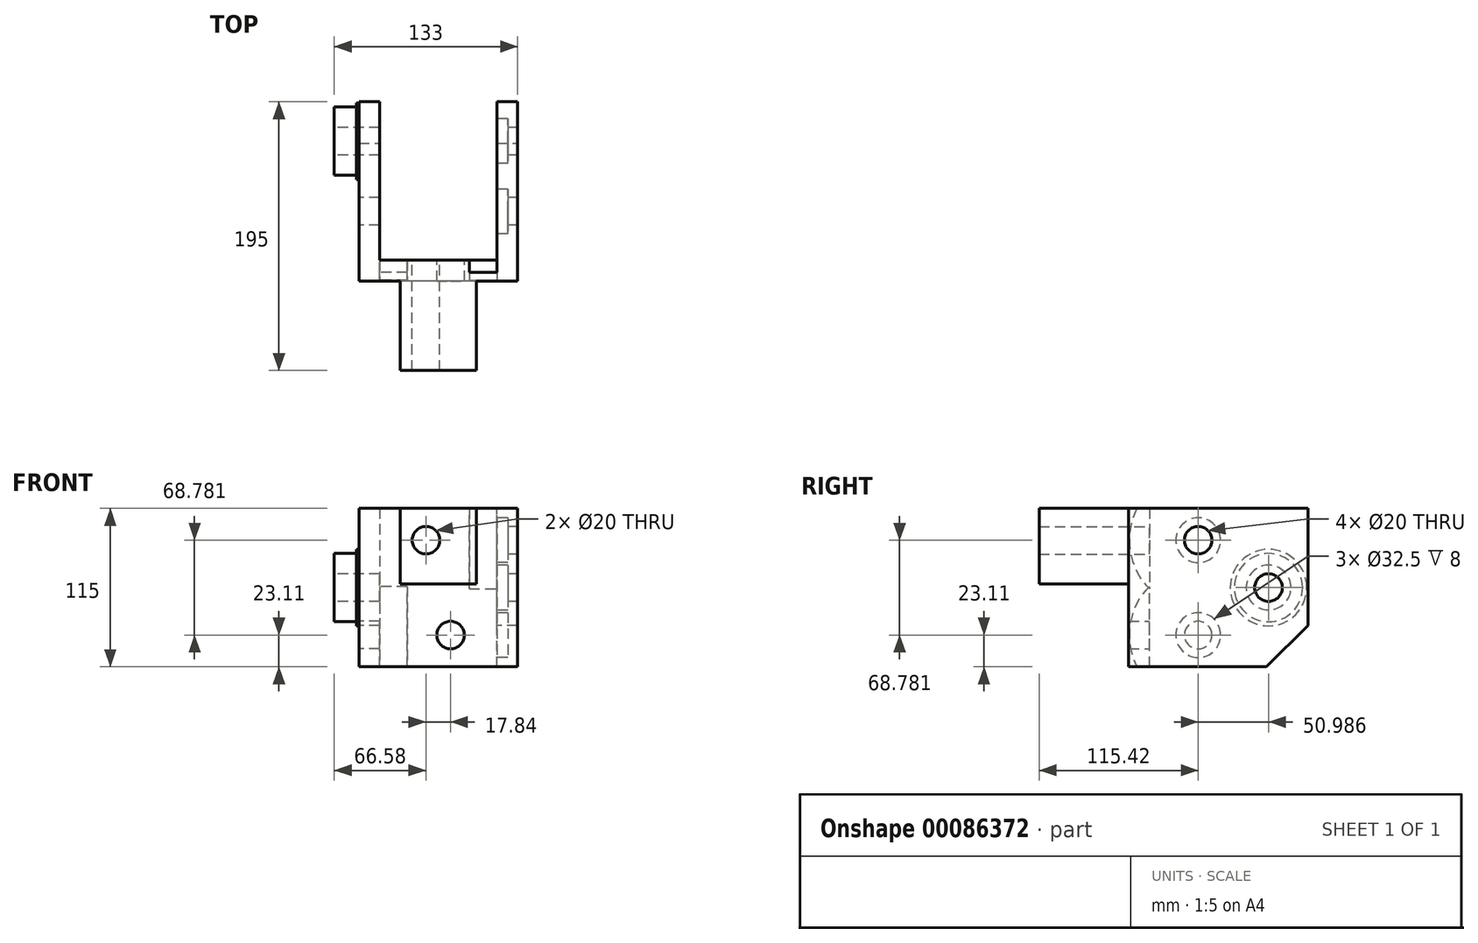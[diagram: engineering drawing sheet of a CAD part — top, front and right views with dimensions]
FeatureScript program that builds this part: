
annotation { "Feature Type Name" : "Feature", "Feature Type Description" : "" }
export const myFeature = defineFeature(function(context is Context, id is Id, definition is map)
    precondition{}
    {
        {
            assignVariable(context, id + "F0", {"name" : "Offset", "anyValue" : 85});
        }
        {
            var Q0;
            Q0=qCreatedBy(makeId("Right.planeOp"),FACE);
            var sketch = newSketch(context, id + "F1", { "sketchPlane" : qUnion([Q0])});
            skCircle(sketch, "E0", {"center": v(0, 0) * mm, "radius": 10 * mm});
            skCircle(sketch, "E1", {"center": v(50.99, 34.4) * mm, "radius": 10 * mm});
            skLineSegment(sketch, "E2.bottom", {"start": v(-35.42, 91.9) * mm, "end": v(79.58, 91.9) * mm});
            skLineSegment(sketch, "E2.top", {"start": v(-35.42, -23.1) * mm, "end": v(79.58, -23.1) * mm});
            skLineSegment(sketch, "E2.left", {"start": v(-35.42, 91.9) * mm, "end": v(-35.42, -23.1) * mm});
            skLineSegment(sketch, "E2.right", {"start": v(79.58, 91.9) * mm, "end": v(79.58, -23.1) * mm});
            skCircle(sketch, "E3", {"center": v(0, 0) * mm, "radius": 61.5 * mm, "construction": true});
            skLineSegment(sketch, "E4", {"start": v(50.99, 34.4) * mm, "end": v(0, 0) * mm});
            skLineSegment(sketch, "E5", {"start": v(79.58, 34.4) * mm, "end": v(50.99, 34.4) * mm, "construction": true});
            skCircle(sketch, "E6", {"center": v(50.99, 34.4) * mm, "radius": 24.75 * mm, "construction": true});
            skCircle(sketch, "E7", {"center": v(0, 0) * mm, "radius": 16.25 * mm, "construction": true});
            skCircle(sketch, "E8.0", {"center": v(0, 0) * mm, "radius": 21.25 * mm, "construction": true});
            skSolve(sketch);
        }
        {
            var Q0;
            Q0 = qSketchRegion(id + "F1", true);
            extrude(context, id + "F2", {"entities" : qUnion([Q0]), "depth" : 15 * mm, "offsetDistance" : 25 * mm});
        }
        {
            var Q0;
            Q0=makeQuery(id+"F2.opExtrude","CAP_FACE",FACE,{"disambiguationData":[OSD([sQuery(id+"F1.wireOp",EDGE,"E0"),sQuery(id+"F1.wireOp",EDGE,"E1"),sQuery(id+"F1.wireOp",EDGE,"E2.bottom"),sQuery(id+"F1.wireOp",EDGE,"E2.top"),sQuery(id+"F1.wireOp",EDGE,"E2.left"),sQuery(id+"F1.wireOp",EDGE,"E2.right")])],"isStart":false});
            cPlane(context, id + "F3", {"entities" : qUnion([Q0]), "cplaneType" : CPlaneType.OFFSET, "offset" : (getVariable(context, 'Offset')) * mm, "width" : 150 * mm, "height" : 150 * mm});
        }
        {
            var Q0;
            Q0=qCreatedBy(id+"F3.planeOp",FACE);
            var sketch = newSketch(context, id + "F4", { "sketchPlane" : qUnion([Q0])});
            skCircle(sketch, "E9.0", {"center": v(50.99, 34.4) * mm, "radius": 10 * mm});
            skCircle(sketch, "E10", {"center": v(0, 68.78) * mm, "radius": 10 * mm});
            skLineSegment(sketch, "E11.bottom", {"start": v(-35.42, -23.1) * mm, "end": v(79.58, -23.1) * mm});
            skLineSegment(sketch, "E11.top", {"start": v(-35.42, 91.9) * mm, "end": v(79.58, 91.9) * mm});
            skLineSegment(sketch, "E11.left", {"start": v(-35.42, -23.1) * mm, "end": v(-35.42, 91.9) * mm});
            skLineSegment(sketch, "E11.right", {"start": v(79.58, -23.1) * mm, "end": v(79.58, 91.9) * mm});
            skCircle(sketch, "E12", {"center": v(50.99, 34.4) * mm, "radius": 61.5 * mm, "construction": true});
            skLineSegment(sketch, "E13", {"start": v(0, 68.78) * mm, "end": v(50.99, 34.4) * mm, "construction": true});
            skSolve(sketch);
        }
        {
            var Q0;
            Q0=makeQuery(id+"F2.opExtrude","SWEPT_FACE",FACE,{"disambiguationData":[OSD([sQuery(id+"F1.wireOp",EDGE,"E2.left")])]});
            var sketch = newSketch(context, id + "F5", { "sketchPlane" : qUnion([Q0])});
            skLineSegment(sketch, "E14", {"start": v(0, -23.1) * mm, "end": v(100, -23.1) * mm});
            skLineSegment(sketch, "E15", {"start": v(100, -23.1) * mm, "end": v(100, 91.9) * mm});
            skLineSegment(sketch, "E16", {"start": v(100, 91.9) * mm, "end": v(0, 91.9) * mm});
            skLineSegment(sketch, "E17", {"start": v(0, 91.9) * mm, "end": v(0, -23.1) * mm});
            skLineSegment(sketch, "E18.0", {"start": v(15, 10) * mm, "end": v(15, -10) * mm, "construction": true});
            skLineSegment(sketch, "E19", {"start": v(16, 0) * mm, "end": v(66.42, 0) * mm, "construction": true});
            skCircle(sketch, "E20", {"center": v(66.42, 0) * mm, "radius": 10 * mm});
            skLineSegment(sketch, "E21", {"start": v(48.58, 68.78) * mm, "end": v(99, 68.78) * mm, "construction": true});
            skLineSegment(sketch, "E22.0", {"start": v(100, 78.78) * mm, "end": v(100, 58.78) * mm, "construction": true});
            skCircle(sketch, "E23", {"center": v(48.58, 68.78) * mm, "radius": 10 * mm});
            skPoint(sketch, "E24", {"position": v(84, 68.78) * mm});
            skLineSegment(sketch, "E25", {"start": v(15, 0) * mm, "end": v(16, 0) * mm});
            skLineSegment(sketch, "E26", {"start": v(100, 68.78) * mm, "end": v(99, 68.78) * mm, "construction": true});
            skSolve(sketch);
        }
        {
            var Q0;
            Q0 = qSketchRegion(id + "F5", true);
            extrude(context, id + "F6", {"entities" : qUnion([Q0]), "operationType" : NewBodyOperationType.ADD, "depth" : 25 * mm, "offsetDistance" : 25 * mm});
        }
        {
            var Q0;
            Q0=makeQuery(id+"F4.imprint","IMPRINT",FACE,{"disambiguationData":[TD([[makeQuery(id+"F4.imprint","IMPRINT",EDGE,{"derivedFrom":sQuery(id+"F4.wireOp",EDGE,"E9.0")}),-1.0]])]});
            var Q1;
            Q1=makeQuery(id+"F6.opExtrude","SWEPT_FACE",FACE,{"disambiguationData":[OSD([sQuery(id+"F5.wireOp",EDGE,"E15"),sQuery(id+"F5.wireOp",EDGE,"E22.0")])]});
            extrude(context, id + "F7", {"entities" : qUnion([Q0, Q1]), "operationType" : NewBodyOperationType.ADD, "depth" : 15 * mm, "offsetDistance" : 25 * mm});
        }
        {
            var Q0;
            Q0=makeQuery(id+"F1.imprint","IMPRINT",FACE,{"disambiguationData":[TD([[makeQuery(id+"F1.imprint","IMPRINT",EDGE,{"derivedFrom":sQuery(id+"F1.wireOp",EDGE,"E0")}),-1.0]])]});
            var sketch = newSketch(context, id + "F8", { "sketchPlane" : qUnion([Q0])});
            skCircle(sketch, "E27.0", {"center": v(50.99, 34.4) * mm, "radius": 24.75 * mm});
            skCircle(sketch, "E28.0", {"center": v(50.99, 34.4) * mm, "radius": 10 * mm});
            skSolve(sketch);
        }
        {
            var Q0;
            Q0 = qSketchRegion(id + "F8", true);
            extrude(context, id + "F9", {"entities" : qUnion([Q0]), "operationType" : NewBodyOperationType.ADD, "oppositeDirection" : true, "depth" : 18 * mm, "offsetDistance" : 25 * mm});
        }
        {
            var Q0;
            Q0=makeQuery(id+"F2.opExtrude","SWEPT_EDGE",EDGE,{"disambiguationData":[OSD([sQuery(id+"F1.wireOp",EDGE,"E2.top"),sQuery(id+"F1.wireOp",EDGE,"E2.right")])]});
            var Q1;
            Q1=makeQuery(id+"F7.opExtrude","SWEPT_EDGE",EDGE,{"disambiguationData":[OSD([sQuery(id+"F4.wireOp",EDGE,"E11.bottom"),sQuery(id+"F4.wireOp",EDGE,"E11.right")])]});
            chamfer(context, id + "F10", {"entities" : qUnion([Q0, Q1]), "width" : 30 * mm, "tangentPropagation" : true});
        }
        {
            var Q0;
            Q0=makeQuery(id+"F1.imprint","IMPRINT",FACE,{"disambiguationData":[TD([[makeQuery(id+"F1.imprint","IMPRINT",EDGE,{"derivedFrom":sQuery(id+"F1.wireOp",EDGE,"E0")}),-1.0]])]});
            var sketch = newSketch(context, id + "F11", { "sketchPlane" : qUnion([Q0])});
            skCircle(sketch, "E29.0", {"center": v(50.99, 34.4) * mm, "radius": 24.75 * mm});
            skCircle(sketch, "E30.0", {"center": v(50.99, 34.4) * mm, "radius": 27.75 * mm});
            skSolve(sketch);
        }
        {
            var Q0;
            Q0 = qSketchRegion(id + "F11", true);
            extrude(context, id + "F12", {"entities" : qUnion([Q0]), "operationType" : NewBodyOperationType.ADD, "oppositeDirection" : true, "depth" : 2 * mm, "offsetDistance" : 25 * mm});
        }
        {
            var Q0;
            Q0=makeQuery(id+"F7.boolean.opBoolean","MERGE",FACE,{"derivedFrom":[makeQuery(id+"F7.opExtrude","CAP_FACE",FACE,{"disambiguationData":[OSD([sQuery(id+"F4.wireOp",EDGE,"E9.0"),sQuery(id+"F4.wireOp",EDGE,"E10"),sQuery(id+"F4.wireOp",EDGE,"E11.bottom"),sQuery(id+"F4.wireOp",EDGE,"E11.top"),sQuery(id+"F4.wireOp",EDGE,"E11.left"),sQuery(id+"F4.wireOp",EDGE,"E11.right")])],"isStart":true}),makeQuery(id+"F7.opExtrude","CAP_FACE",FACE,{"disambiguationData":[OSD([sQuery(id+"F5.wireOp",EDGE,"E15")])],"isStart":true})]});
            var Q1;
            Q1=makeQuery(id+"F2.opExtrude","CAP_FACE",FACE,{"disambiguationData":[OSD([sQuery(id+"F1.wireOp",EDGE,"E0"),sQuery(id+"F1.wireOp",EDGE,"E1"),sQuery(id+"F1.wireOp",EDGE,"E2.bottom"),sQuery(id+"F1.wireOp",EDGE,"E2.top"),sQuery(id+"F1.wireOp",EDGE,"E2.left"),sQuery(id+"F1.wireOp",EDGE,"E2.right")])],"isStart":false});
            cPlane(context, id + "F13", {"entities" : qUnion([Q0, Q1]), "cplaneType" : CPlaneType.MID_PLANE, "offset" : 25 * mm, "width" : 150 * mm, "height" : 150 * mm});
        }
        {
            var Q0;
            Q0=makeQuery(id+"F7.boolean.opBoolean","MERGE",FACE,{"derivedFrom":[makeQuery(id+"F7.opExtrude","CAP_FACE",FACE,{"disambiguationData":[OSD([sQuery(id+"F4.wireOp",EDGE,"E9.0"),sQuery(id+"F4.wireOp",EDGE,"E10"),sQuery(id+"F4.wireOp",EDGE,"E11.bottom"),sQuery(id+"F4.wireOp",EDGE,"E11.top"),sQuery(id+"F4.wireOp",EDGE,"E11.left"),sQuery(id+"F4.wireOp",EDGE,"E11.right")])],"isStart":true}),makeQuery(id+"F7.opExtrude","CAP_FACE",FACE,{"disambiguationData":[OSD([sQuery(id+"F5.wireOp",EDGE,"E15")])],"isStart":true})]});
            var sketch = newSketch(context, id + "F14", { "sketchPlane" : qUnion([Q0])});
            skCircle(sketch, "E31", {"center": v(0, 68.78) * mm, "radius": 16.25 * mm});
            skCircle(sketch, "E32", {"center": v(-50.99, 34.4) * mm, "radius": 16.25 * mm});
            skCircle(sketch, "E33.0", {"center": v(0, 0) * mm, "radius": 10 * mm, "construction": true});
            skCircle(sketch, "E34", {"center": v(0, 0) * mm, "radius": 16.25 * mm});
            skSolve(sketch);
        }
        {
            var Q0;
            Q0 = qSketchRegion(id + "F14", true);
            var Q1;
            Q1=sQuery(id+"F14.wireOp",EDGE,"E31");
            extrude(context, id + "F15", {"entities" : qUnion([Q0]), "operationType" : NewBodyOperationType.REMOVE, "surfaceEntities" : qUnion([Q1]), "oppositeDirection" : true, "depth" : 8 * mm, "offsetDistance" : 25 * mm});
        }
        {
            var Q0;
            Q0=makeQuery(id+"F7.boolean.opBoolean","MERGE",FACE,{"derivedFrom":[makeQuery(id+"F7.opExtrude","CAP_FACE",FACE,{"disambiguationData":[OSD([sQuery(id+"F4.wireOp",EDGE,"E9.0"),sQuery(id+"F4.wireOp",EDGE,"E10"),sQuery(id+"F4.wireOp",EDGE,"E11.bottom"),sQuery(id+"F4.wireOp",EDGE,"E11.top"),sQuery(id+"F4.wireOp",EDGE,"E11.left"),sQuery(id+"F4.wireOp",EDGE,"E11.right")])],"isStart":true}),makeQuery(id+"F7.opExtrude","CAP_FACE",FACE,{"disambiguationData":[OSD([sQuery(id+"F5.wireOp",EDGE,"E15")])],"isStart":true})]});
            var sketch = newSketch(context, id + "F16", { "sketchPlane" : qUnion([Q0])});
            skCircle(sketch, "E35", {"center": v(0, 68.78) * mm, "radius": 50 * mm});
            skSolve(sketch);
        }
        {
            var Q0;
            Q0 = qSketchRegion(id + "F16", true);
            extrude(context, id + "F17", {"entities" : qUnion([Q0]), "operationType" : NewBodyOperationType.REMOVE, "depth" : 20 * mm, "offsetDistance" : 25 * mm});
        }
        {
            var Q0;
            Q0=makeQuery(id+"F2.opExtrude","CAP_FACE",FACE,{"disambiguationData":[OSD([sQuery(id+"F1.wireOp",EDGE,"E0"),sQuery(id+"F1.wireOp",EDGE,"E1"),sQuery(id+"F1.wireOp",EDGE,"E2.bottom"),sQuery(id+"F1.wireOp",EDGE,"E2.top"),sQuery(id+"F1.wireOp",EDGE,"E2.left"),sQuery(id+"F1.wireOp",EDGE,"E2.right")])],"isStart":false});
            var sketch = newSketch(context, id + "F18", { "sketchPlane" : qUnion([Q0])});
            skCircle(sketch, "E36", {"center": v(0, 0) * mm, "radius": 50 * mm});
            skSolve(sketch);
        }
        {
            var Q0;
            Q0 = qSketchRegion(id + "F18", true);
            extrude(context, id + "F19", {"entities" : qUnion([Q0]), "operationType" : NewBodyOperationType.REMOVE, "depth" : 20 * mm, "offsetDistance" : 25 * mm});
        }
        {
            var Q0;
            {var subQ0=sQuery(id+"F5.wireOp",EDGE,"E15");Q0=makeQuery(id+"F7.boolean.opBoolean","MERGE",FACE,{"derivedFrom":[makeQuery(id+"F6.opExtrude","CAP_FACE",FACE,{"disambiguationData":[OSD([sQuery(id+"F5.wireOp",EDGE,"E14"),subQ0,sQuery(id+"F5.wireOp",EDGE,"E16"),sQuery(id+"F5.wireOp",EDGE,"E17"),sQuery(id+"F5.wireOp",EDGE,"E20"),sQuery(id+"F5.wireOp",EDGE,"E23")])],"isStart":false}),makeQuery(id+"F7.opExtrude","SWEPT_FACE",FACE,{"disambiguationData":[OSD([subQ0]),TDD([makeQuery(id+"F6.opExtrude","CAP_EDGE",EDGE,{"disambiguationData":[OSD([subQ0])],"isStart":false})])]})]});}
            var sketch = newSketch(context, id + "F20", { "sketchPlane" : qUnion([Q0])});
            skLineSegment(sketch, "E37.0", {"start": v(115, -23.1) * mm, "end": v(115, 91.9) * mm});
            skLineSegment(sketch, "E38.0", {"start": v(115, -23.1) * mm, "end": v(0, -23.1) * mm});
            skLineSegment(sketch, "E39.0", {"start": v(0, 91.9) * mm, "end": v(0, -23.1) * mm});
            skLineSegment(sketch, "E40.0", {"start": v(115, 91.9) * mm, "end": v(0, 91.9) * mm});
            skSolve(sketch);
        }
        {
            var Q0;
            Q0=makeQuery(id+"F20.imprint","IMPRINT",FACE,{"disambiguationData":[TD([[makeQuery(id+"F20.imprint","IMPRINT",EDGE,{"derivedFrom":sQuery(id+"F20.wireOp",EDGE,"E37.0")}),1.0]])]});
            extrude(context, id + "F21", {"entities" : qUnion([Q0]), "operationType" : NewBodyOperationType.ADD, "depth" : 55 * mm, "offsetDistance" : 25 * mm});
        }
        {
            var Q0;
            Q0=makeQuery(id+"F21.opExtrude","CAP_FACE",FACE,{"disambiguationData":[OSD([sQuery(id+"F5.wireOp",EDGE,"E20"),sQuery(id+"F5.wireOp",EDGE,"E23"),sQuery(id+"F20.wireOp",EDGE,"E37.0"),sQuery(id+"F20.wireOp",EDGE,"E38.0"),sQuery(id+"F20.wireOp",EDGE,"E39.0"),sQuery(id+"F20.wireOp",EDGE,"E40.0")])],"isStart":false});
            var sketch = newSketch(context, id + "F22", { "sketchPlane" : qUnion([Q0])});
            skLineSegment(sketch, "E41.bottom", {"start": v(30, -23.1) * mm, "end": v(85, -23.1) * mm});
            skLineSegment(sketch, "E41.top", {"start": v(30, 91.9) * mm, "end": v(85, 91.9) * mm});
            skLineSegment(sketch, "E41.left", {"start": v(30, -23.1) * mm, "end": v(30, 91.9) * mm});
            skLineSegment(sketch, "E41.right", {"start": v(85, -23.1) * mm, "end": v(85, 91.9) * mm});
            skPoint(sketch, "E41.middle", {"position": v(57.5, 34.4) * mm});
            skLineSegment(sketch, "E42", {"start": v(85, 36.9) * mm, "end": v(30, 36.9) * mm});
            skPoint(sketch, "E43", {"position": v(57.5, -23.1) * mm});
            skSolve(sketch);
        }
        {
            var Q0;
            {var subQ1=makeQuery(id+"F21.opExtrude","CAP_EDGE",EDGE,{"disambiguationData":[OSD([sQuery(id+"F20.wireOp",EDGE,"E37.0")])],"isStart":false});Q0=makeQuery(id+"F22.imprint","IMPRINT",FACE,{"disambiguationData":[TD([[makeQuery(id+"F22.imprint","IMPRINT",EDGE,{"derivedFrom":subQ1}),1.0]])]});}
            var Q1;
            {var subQ2=sQuery(id+"F22.wireOp",EDGE,"E41.bottom");Q1=makeQuery(id+"F22.imprint","IMPRINT",FACE,{"disambiguationData":[TD([[makeQuery(id+"F22.imprint","IMPRINT",EDGE,{"derivedFrom":subQ2}),-1.0]])]});}
            var Q2;
            {var subQ0=makeQuery(id+"F21.opExtrude","CAP_EDGE",EDGE,{"disambiguationData":[OSD([sQuery(id+"F20.wireOp",EDGE,"E39.0")])],"isStart":false});Q2=makeQuery(id+"F22.imprint","IMPRINT",FACE,{"disambiguationData":[TD([[makeQuery(id+"F22.imprint","IMPRINT",EDGE,{"derivedFrom":subQ0}),1.0]])]});}
            extrude(context, id + "F23", {"entities" : qUnion([Q0, Q1, Q2]), "operationType" : NewBodyOperationType.REMOVE, "oppositeDirection" : true, "depth" : 65 * mm, "offsetDistance" : 25 * mm});
        }
    });
